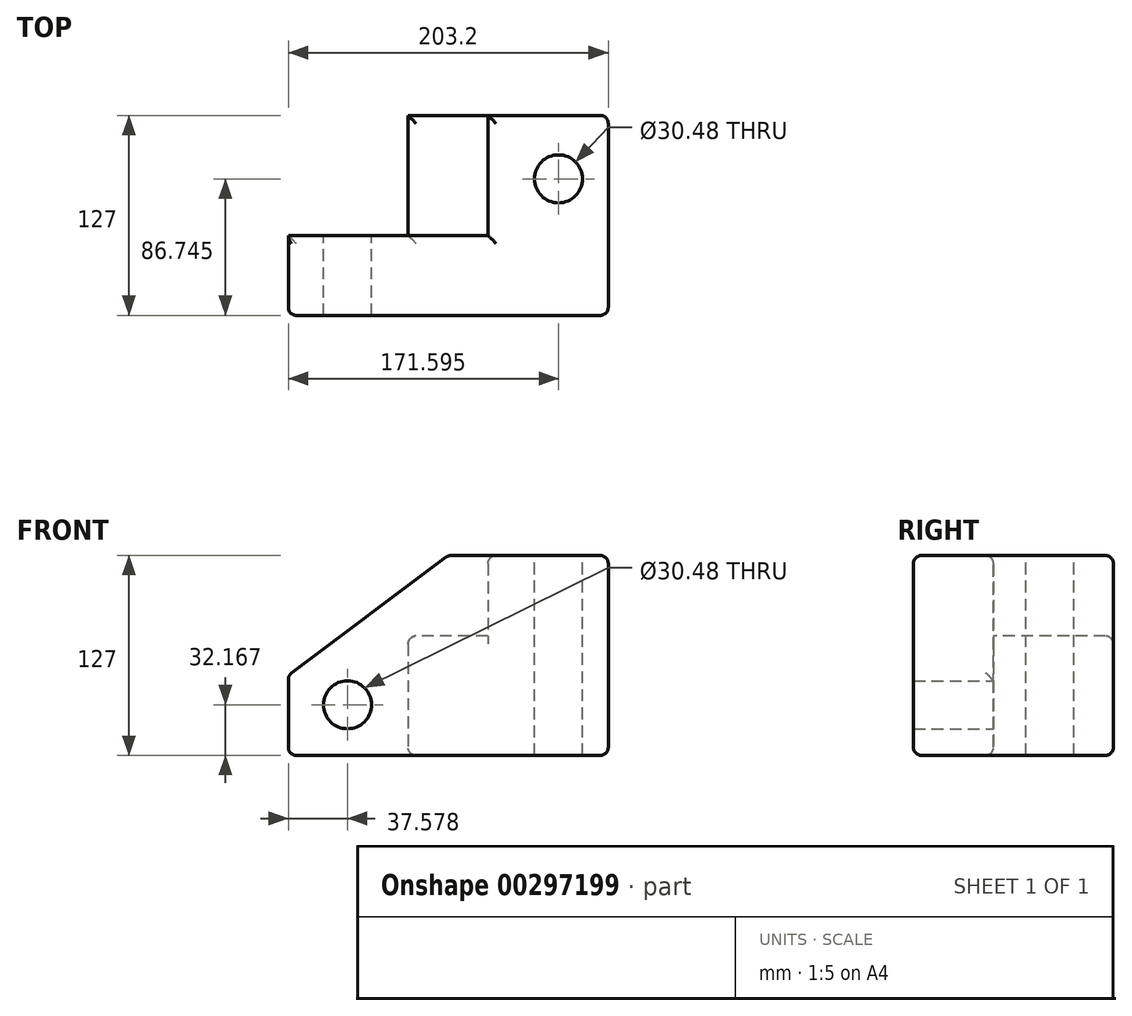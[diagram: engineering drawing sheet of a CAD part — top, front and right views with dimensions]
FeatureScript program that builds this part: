
annotation { "Feature Type Name" : "Feature", "Feature Type Description" : "" }
export const myFeature = defineFeature(function(context is Context, id is Id, definition is map)
    precondition{}
    {
        {
            var Q0;
            Q0=qCreatedBy(makeId("Front.planeOp"),FACE);
            var sketch = newSketch(context, id + "F0", { "sketchPlane" : qUnion([Q0])});
            skLineSegment(sketch, "E0.bottom", {"start": v(101.6, -63.5) * mm, "end": v(-101.6, -63.5) * mm});
            skLineSegment(sketch, "E0.top", {"start": v(101.6, 63.5) * mm, "end": v(-101.6, 63.5) * mm});
            skLineSegment(sketch, "E0.left", {"start": v(101.6, -63.5) * mm, "end": v(101.6, 63.5) * mm});
            skLineSegment(sketch, "E0.right", {"start": v(-101.6, -63.5) * mm, "end": v(-101.6, 63.5) * mm});
            skPoint(sketch, "E0.middle", {"position": v(0, 0) * mm});
            skSolve(sketch);
        }
        {
            var Q0;
            Q0=makeQuery(id+"F0.imprint","IMPRINT",FACE,{"disambiguationData":[TD([[makeQuery(id+"F0.imprint","IMPRINT",EDGE,{"derivedFrom":sQuery(id+"F0.wireOp",EDGE,"E0.bottom")}),-1.0]])]});
            extrude(context, id + "F1", {"entities" : qUnion([Q0]), "depth" : 127 * mm});
        }
        {
            var Q0;
            Q0=qCreatedBy(makeId("Front.planeOp"),FACE);
            var sketch = newSketch(context, id + "F2", { "sketchPlane" : qUnion([Q0])});
            skLineSegment(sketch, "E1", {"start": v(-101.79, 63.15) * mm, "end": v(25.21, 63.15) * mm});
            skLineSegment(sketch, "E2", {"start": v(25.21, 63.15) * mm, "end": v(25.21, 12.35) * mm});
            skLineSegment(sketch, "E3", {"start": v(25.21, 12.35) * mm, "end": v(-25.59, 12.35) * mm});
            skLineSegment(sketch, "E4", {"start": v(-25.59, 12.35) * mm, "end": v(-25.59, -63.85) * mm});
            skLineSegment(sketch, "E5", {"start": v(-25.59, -63.85) * mm, "end": v(-101.79, -63.85) * mm});
            skLineSegment(sketch, "E6", {"start": v(-101.79, -63.85) * mm, "end": v(-101.79, 63.15) * mm});
            skSolve(sketch);
        }
        {
            var Q0;
            Q0 = qSketchRegion(id + "F2", true);
            extrude(context, id + "F3", {"entities" : qUnion([Q0]), "operationType" : NewBodyOperationType.REMOVE, "oppositeDirection" : true, "depth" : 76.2 * mm, "hasSecondDirection" : true, "secondDirectionOppositeDirection" : false, "secondDirectionDepth" : 76.2 * mm});
        }
        {
            var Q0;
            Q0=makeQuery(id+"F3.boolean.opBoolean","COPY",FACE,{"derivedFrom":makeQuery(id+"F3.opExtrude","SWEPT_FACE",FACE,{"disambiguationData":[OSD([sQuery(id+"F2.wireOp",EDGE,"E1")])]})});
            extrude(context, id + "F4", {"entities" : qUnion([Q0]), "operationType" : NewBodyOperationType.REMOVE, "oppositeDirection" : true, "depth" : 25.4 * mm});
        }
        {
            var Q0;
            Q0=makeQuery(id+"F1.opExtrude","SWEPT_EDGE",EDGE,{"disambiguationData":[OSD([sQuery(id+"F0.wireOp",EDGE,"E0.top"),sQuery(id+"F0.wireOp",EDGE,"E0.right")])]});
            chamfer(context, id + "F5", {"entities" : qUnion([Q0]), "chamferType" : ChamferType.TWO_OFFSETS, "width1" : 76.2 * mm, "oppositeDirection" : false, "width2" : 101.6 * mm, "tangentPropagation" : true});
        }
        {
            var Q0;
            {var subQ0=sQuery(id+"F2.wireOp",EDGE,"E2");var subQ1=sQuery(id+"F0.wireOp",EDGE,"E0.right");var subQ2=sQuery(id+"F0.wireOp",EDGE,"E0.left");var subQ3=sQuery(id+"F0.wireOp",EDGE,"E0.top");var subQ4=sQuery(id+"F0.wireOp",EDGE,"E0.bottom");Q0=makeQuery(id+"F4.boolean.opBoolean","MERGE",EDGE,{"derivedFrom":[makeQuery(id+"F3.boolean.opBoolean","INTERSECT",EDGE,{"derivedFrom":[makeQuery(id+"F1.opExtrude","CAP_FACE",FACE,{"disambiguationData":[OSD([subQ4,subQ3,subQ2,subQ1])],"isStart":true}),makeQuery(id+"F3.opExtrude","SWEPT_FACE",FACE,{"disambiguationData":[OSD([subQ0])]})]}),makeQuery(id+"F4.opExtrude","SWEPT_EDGE",EDGE,{"disambiguationData":[OSD([subQ4,subQ3,subQ2,subQ1,sQuery(id+"F2.wireOp",EDGE,"E1"),subQ0])]})]});}
            var Q1;
            Q1=makeQuery(id+"F4.boolean.opBoolean","INTERSECT",EDGE,{"derivedFrom":[makeQuery(id+"F1.opExtrude","SWEPT_FACE",FACE,{"disambiguationData":[OSD([sQuery(id+"F0.wireOp",EDGE,"E0.top")])]}),makeQuery(id+"F4.opExtrude","SWEPT_FACE",FACE,{"disambiguationData":[OSD([sQuery(id+"F2.wireOp",EDGE,"E1"),sQuery(id+"F2.wireOp",EDGE,"E2")])]})]});
            var Q2;
            Q2=makeQuery(id+"F1.opExtrude","CAP_EDGE",EDGE,{"disambiguationData":[OSD([sQuery(id+"F0.wireOp",EDGE,"E0.top")])],"isStart":true});
            var Q3;
            Q3=makeQuery(id+"F3.boolean.opBoolean","INTERSECT",EDGE,{"derivedFrom":[makeQuery(id+"F1.opExtrude","CAP_FACE",FACE,{"disambiguationData":[OSD([sQuery(id+"F0.wireOp",EDGE,"E0.bottom"),sQuery(id+"F0.wireOp",EDGE,"E0.top"),sQuery(id+"F0.wireOp",EDGE,"E0.left"),sQuery(id+"F0.wireOp",EDGE,"E0.right")])],"isStart":true}),makeQuery(id+"F3.opExtrude","SWEPT_FACE",FACE,{"disambiguationData":[OSD([sQuery(id+"F2.wireOp",EDGE,"E3")])]})]});
            var Q4;
            Q4=makeQuery(id+"F3.boolean.opBoolean","COPY",EDGE,{"derivedFrom":makeQuery(id+"F3.opExtrude","SWEPT_EDGE",EDGE,{"disambiguationData":[OSD([sQuery(id+"F2.wireOp",EDGE,"E3"),sQuery(id+"F2.wireOp",EDGE,"E4")])]})});
            var Q5;
            {var subQ0=sQuery(id+"F0.wireOp",EDGE,"E0.right");Q5=makeQuery(id+"F5.opChamfer","BLEND_EDGE",EDGE,{"blendedFrom":[makeQuery(id+"F1.opExtrude","SWEPT_EDGE",EDGE,{"disambiguationData":[OSD([sQuery(id+"F0.wireOp",EDGE,"E0.top"),subQ0])]}),makeQuery(id+"F1.opExtrude","SWEPT_FACE",FACE,{"disambiguationData":[OSD([subQ0])]})],"blendedInto":[makeQuery(id+"F1.opExtrude","SWEPT_FACE",FACE,{"disambiguationData":[OSD([subQ0])]})]});}
            var Q6;
            {var subQ0=sQuery(id+"F0.wireOp",EDGE,"E0.top");Q6=makeQuery(id+"F5.opChamfer","BLEND_EDGE",EDGE,{"blendedFrom":[makeQuery(id+"F1.opExtrude","SWEPT_EDGE",EDGE,{"disambiguationData":[OSD([subQ0,sQuery(id+"F0.wireOp",EDGE,"E0.right")])]}),makeQuery(id+"F1.opExtrude","SWEPT_FACE",FACE,{"disambiguationData":[OSD([subQ0])]})],"blendedInto":[makeQuery(id+"F1.opExtrude","SWEPT_FACE",FACE,{"disambiguationData":[OSD([subQ0])]})]});}
            var Q7;
            Q7=makeQuery(id+"F4.boolean.opBoolean","INTERSECT",EDGE,{"derivedFrom":[makeQuery(id+"F1.opExtrude","SWEPT_FACE",FACE,{"disambiguationData":[OSD([sQuery(id+"F0.wireOp",EDGE,"E0.top")])]}),makeQuery(id+"F4.opExtrude","SWEPT_FACE",FACE,{"disambiguationData":[OSD([sQuery(id+"F2.wireOp",EDGE,"E1")])]})]});
            var Q8;
            Q8=makeQuery(id+"F1.opExtrude","CAP_EDGE",EDGE,{"disambiguationData":[OSD([sQuery(id+"F0.wireOp",EDGE,"E0.left")])],"isStart":true});
            var Q9;
            Q9=makeQuery(id+"F1.opExtrude","CAP_EDGE",EDGE,{"disambiguationData":[OSD([sQuery(id+"F0.wireOp",EDGE,"E0.bottom")])],"isStart":true});
            var Q10;
            Q10=makeQuery(id+"F3.boolean.opBoolean","INTERSECT",EDGE,{"derivedFrom":[makeQuery(id+"F1.opExtrude","SWEPT_FACE",FACE,{"disambiguationData":[OSD([sQuery(id+"F0.wireOp",EDGE,"E0.bottom")])]}),makeQuery(id+"F3.opExtrude","SWEPT_FACE",FACE,{"disambiguationData":[OSD([sQuery(id+"F2.wireOp",EDGE,"E4")])]})]});
            var Q11;
            Q11=makeQuery(id+"F3.boolean.opBoolean","INTERSECT",EDGE,{"derivedFrom":[makeQuery(id+"F1.opExtrude","SWEPT_FACE",FACE,{"disambiguationData":[OSD([sQuery(id+"F0.wireOp",EDGE,"E0.bottom")])]}),makeQuery(id+"F3.opExtrude","CAP_FACE",FACE,{"disambiguationData":[OSD([sQuery(id+"F2.wireOp",EDGE,"E1"),sQuery(id+"F2.wireOp",EDGE,"E2"),sQuery(id+"F2.wireOp",EDGE,"E3"),sQuery(id+"F2.wireOp",EDGE,"E4"),sQuery(id+"F2.wireOp",EDGE,"E5"),sQuery(id+"F2.wireOp",EDGE,"E6")])],"isStart":true})]});
            var Q12;
            Q12=makeQuery(id+"F1.opExtrude","SWEPT_EDGE",EDGE,{"disambiguationData":[OSD([sQuery(id+"F0.wireOp",EDGE,"E0.bottom"),sQuery(id+"F0.wireOp",EDGE,"E0.right")])]});
            var Q13;
            Q13=makeQuery(id+"F1.opExtrude","CAP_FACE",FACE,{"disambiguationData":[OSD([sQuery(id+"F0.wireOp",EDGE,"E0.bottom"),sQuery(id+"F0.wireOp",EDGE,"E0.top"),sQuery(id+"F0.wireOp",EDGE,"E0.left"),sQuery(id+"F0.wireOp",EDGE,"E0.right")])],"isStart":false});
            var Q14;
            {var subQ0=sQuery(id+"F2.wireOp",EDGE,"E1");Q14=makeQuery(id+"F5.opChamfer","BLEND_EDGE",EDGE,{"blendedFrom":[makeQuery(id+"F1.opExtrude","SWEPT_EDGE",EDGE,{"disambiguationData":[OSD([sQuery(id+"F0.wireOp",EDGE,"E0.top"),sQuery(id+"F0.wireOp",EDGE,"E0.right")])]}),makeQuery(id+"F4.boolean.opBoolean","MERGE",FACE,{"derivedFrom":[makeQuery(id+"F3.boolean.opBoolean","COPY",FACE,{"derivedFrom":makeQuery(id+"F3.opExtrude","CAP_FACE",FACE,{"disambiguationData":[OSD([subQ0,sQuery(id+"F2.wireOp",EDGE,"E2"),sQuery(id+"F2.wireOp",EDGE,"E3"),sQuery(id+"F2.wireOp",EDGE,"E4"),sQuery(id+"F2.wireOp",EDGE,"E5"),sQuery(id+"F2.wireOp",EDGE,"E6")])],"isStart":true})}),makeQuery(id+"F4.opExtrude","SWEPT_FACE",FACE,{"disambiguationData":[OSD([subQ0])]})]})],"blendedInto":[makeQuery(id+"F4.boolean.opBoolean","MERGE",FACE,{"derivedFrom":[makeQuery(id+"F3.boolean.opBoolean","COPY",FACE,{"derivedFrom":makeQuery(id+"F3.opExtrude","CAP_FACE",FACE,{"disambiguationData":[OSD([subQ0,sQuery(id+"F2.wireOp",EDGE,"E2"),sQuery(id+"F2.wireOp",EDGE,"E3"),sQuery(id+"F2.wireOp",EDGE,"E4"),sQuery(id+"F2.wireOp",EDGE,"E5"),sQuery(id+"F2.wireOp",EDGE,"E6")])],"isStart":true})}),makeQuery(id+"F4.opExtrude","SWEPT_FACE",FACE,{"disambiguationData":[OSD([subQ0])]})]})]});}
            var Q15;
            Q15=makeQuery(id+"F1.opExtrude","SWEPT_EDGE",EDGE,{"disambiguationData":[OSD([sQuery(id+"F0.wireOp",EDGE,"E0.top"),sQuery(id+"F0.wireOp",EDGE,"E0.left")])]});
            var Q16;
            Q16=makeQuery(id+"F1.opExtrude","SWEPT_EDGE",EDGE,{"disambiguationData":[OSD([sQuery(id+"F0.wireOp",EDGE,"E0.bottom"),sQuery(id+"F0.wireOp",EDGE,"E0.left")])]});
            fillet(context, id + "F6", {"entities" : qUnion([Q0, Q1, Q2, Q3, Q4, Q5, Q6, Q7, Q8, Q9, Q10, Q11, Q12, Q13, Q14, Q15, Q16]), "radius" : 5.08 * mm, "tangentPropagation" : true, "allowEdgeOverflow" : false});
        }
        {
            var Q0;
            {var subQ0=sQuery(id+"F2.wireOp",EDGE,"E1");Q0=makeQuery(id+"F4.boolean.opBoolean","MERGE",FACE,{"derivedFrom":[makeQuery(id+"F3.boolean.opBoolean","COPY",FACE,{"derivedFrom":makeQuery(id+"F3.opExtrude","CAP_FACE",FACE,{"disambiguationData":[OSD([subQ0,sQuery(id+"F2.wireOp",EDGE,"E2"),sQuery(id+"F2.wireOp",EDGE,"E3"),sQuery(id+"F2.wireOp",EDGE,"E4"),sQuery(id+"F2.wireOp",EDGE,"E5"),sQuery(id+"F2.wireOp",EDGE,"E6")])],"isStart":true})}),makeQuery(id+"F4.opExtrude","SWEPT_FACE",FACE,{"disambiguationData":[OSD([subQ0])]})]});}
            var sketch = newSketch(context, id + "F7", { "sketchPlane" : qUnion([Q0])});
            skCircle(sketch, "E7", {"center": v(64.02, -31.33) * mm, "radius": 15.24 * mm});
            skSolve(sketch);
        }
        {
            var Q0;
            Q0=makeQuery(id+"F7.imprint","IMPRINT",FACE,{"disambiguationData":[TD([[makeQuery(id+"F7.imprint","IMPRINT",EDGE,{"derivedFrom":sQuery(id+"F7.wireOp",EDGE,"E7")}),1.0]])]});
            var Q1;
            Q1=sQuery(id+"F7.wireOp",EDGE,"E7");
            extrude(context, id + "F8", {"entities" : qUnion([Q0]), "operationType" : NewBodyOperationType.REMOVE, "surfaceEntities" : qUnion([Q1]), "oppositeDirection" : true, "depth" : 51.05 * mm});
        }
        {
            var Q0;
            Q0=makeQuery(id+"F1.opExtrude","SWEPT_FACE",FACE,{"disambiguationData":[OSD([sQuery(id+"F0.wireOp",EDGE,"E0.top")])]});
            var sketch = newSketch(context, id + "F9", { "sketchPlane" : qUnion([Q0])});
            skCircle(sketch, "E8", {"center": v(70, -40.26) * mm, "radius": 15.24 * mm});
            skSolve(sketch);
        }
        {
            var Q0;
            Q0=makeQuery(id+"F9.imprint","IMPRINT",FACE,{"disambiguationData":[TD([[makeQuery(id+"F9.imprint","IMPRINT",EDGE,{"derivedFrom":sQuery(id+"F9.wireOp",EDGE,"E8")}),1.0]])]});
            var Q1;
            Q1=sQuery(id+"F9.wireOp",EDGE,"E8");
            extrude(context, id + "F10", {"entities" : qUnion([Q0]), "operationType" : NewBodyOperationType.REMOVE, "surfaceEntities" : qUnion([Q1]), "oppositeDirection" : true, "depth" : 128.27 * mm});
        }
    });
